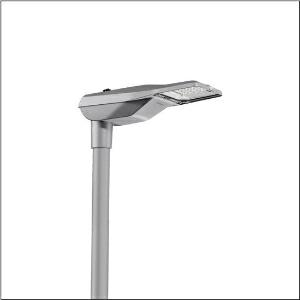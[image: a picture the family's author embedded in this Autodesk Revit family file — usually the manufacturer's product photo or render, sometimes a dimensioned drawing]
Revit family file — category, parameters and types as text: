
# Revit family: streetlight_sl_21_micro___pl52_5xe1h43s08db_6aa2
name_source: partatom
category: Lighting Fixtures
units: mm (PartAtom-declared; Revit-internal decimal feet)

## family parameters
Cut with Voids When Loaded = No
Host = Face
Light Source = No
Part Type = Normal
Room Calculation Point = No
Round Connector Dimension = Use Diameter
Shared = No

## types (1)
- --- (1 x LED, 5230 lm, 39.1 W, 4000K)
    Apparent Load = 39 VA
    CIE Flux Codes = 27 59 98 100 100
    Color Rendering = 70
    Color Temperature = 4000K
    Default Elevation = 1800 mm
    Description = Streetlight SL 21 micro, mast luminaire, primary light control with lens, of PMMA, primary optical cover: cover, of toughened safety glass, transparent, light distribution: PL52, light emission: direct distribution, primary light characteristic: asymmetric, installation type: side-entry, post-top, LED, High Power LED, rated luminous flux: 5.230lm, luminous efficacy: 134lm/W, light colour: 740, colour temperature: 4000K, control: flexible luminous flux parameterisation, time-dependent luminous flux control, constant luminous flux control, overheat protection, pre-setting: logarithmic dimming characteristic, mains connection: 220..240V, AC, 50/60Hz, start of lifetime: 39W, end of service life: 41W, reduction: 18W, luminaire housing, of diecast aluminium, powder-coated, Siteco® metallic grey (DB 702S), corrosivity category C5 mid according to DIN EN ISO 12944, please order mast flange separately, inclination adjustable: 0°, 5°, 10°, 15°, sealing non-destructively replaceable, multi-level sealing system, length: 528mm, width: 235mm, height: 110mm, mast flange for spigot size: 42mm (side-entry): 5XC10008XM4, 60/48mm (side-entry/post-top): 5XC10108XM2, 76/60mm (side-entry/post-top): 5XC10108XM1, Smart Interface above, protection rating (complete): IP66, insulation class (complete): insulation class II (safety insulation), certification: CE, ENEC, ENEC+, VDE, impact resistance: IK09, permissible operating ambient temperature for outdoor applications: -40..+50°C, standard-compliant lighting for roads and squares, packaging unit: 1 piece

Light Distribution: PL52
    Height = 110 mm
    Lamp = 1 x LED
    Lamp Light Flux = 5230 lm
    Lamp Power = 39.1 W
    Lamp count = 1
    Length = 528 mm
    Luminous efficacy = 134 lm/W
    Manufacturer = Siteco
    ModVariant = No
    Model = 5XE1H43S08DB
    Number of Poles = 1
    OnlyDefault = Yes
    Power Factor = 1
    Product Name = Streetlight SL 21 micro | PL52
    Product group = mast luminaire | pylon top
    ProductGroupID = 6100
    Protection Class = Protection class II
    Protection Degree = IP 66
    RLX_Detail_Level = 1
    RLX_Emergency_Light_Flux = 0 lm
    RLX_Emergency_Type = 0
    RLX_Emergency_Type_DB = No
    RlxData = <blob elided: 107553 chars, md5=29cc3aef>
    Socket = socket
    Standby Power = 0 W
    System Light Flux = 5230 lm
    System Power = 39 W
    Type Comments = factory setting: luminous flux: 100 % | dim-lin: 254 | 765 mA
    Type Image = l_1277292.jpg
    URL = http://relux.com
    VarID = @adj_126583
    Voltage = 0 V
    Weight = 0.00 kg
    Width = 235 mm

## geometry (parser evidence)
native form markers: Blend x4, Sweep x10
no freeform markers — native parametric forms only
